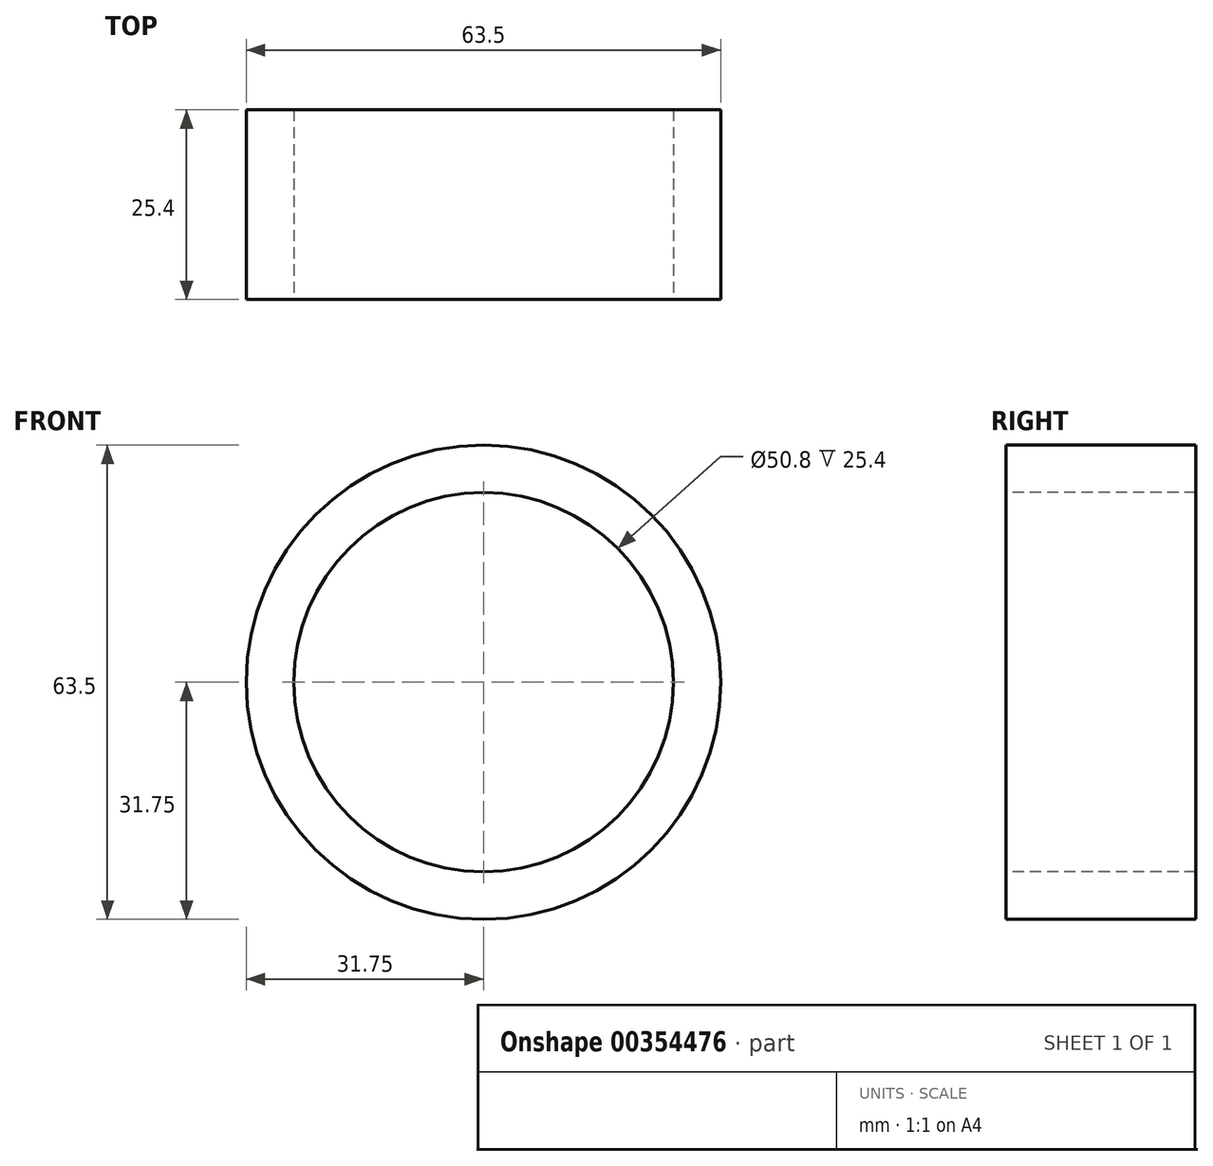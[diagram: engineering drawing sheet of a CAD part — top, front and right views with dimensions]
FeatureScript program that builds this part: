
annotation { "Feature Type Name" : "Feature", "Feature Type Description" : "" }
export const myFeature = defineFeature(function(context is Context, id is Id, definition is map)
    precondition{}
    {
        {
            var Q0;
            Q0=qCreatedBy(makeId("Front.planeOp"),FACE);
            var sketch = newSketch(context, id + "F0", { "sketchPlane" : qUnion([Q0])});
            skCircle(sketch, "E0", {"center": v(0, 0) * mm, "radius": 25.4 * mm});
            skCircle(sketch, "E1", {"center": v(0, 0) * mm, "radius": 31.75 * mm});
            skSolve(sketch);
        }
        {
            var Q0;
            Q0 = qSketchRegion(id + "F0", true);
            extrude(context, id + "F1", {"entities" : qUnion([Q0]), "oppositeDirection" : true, "depth" : 25.4 * mm});
        }
    });
